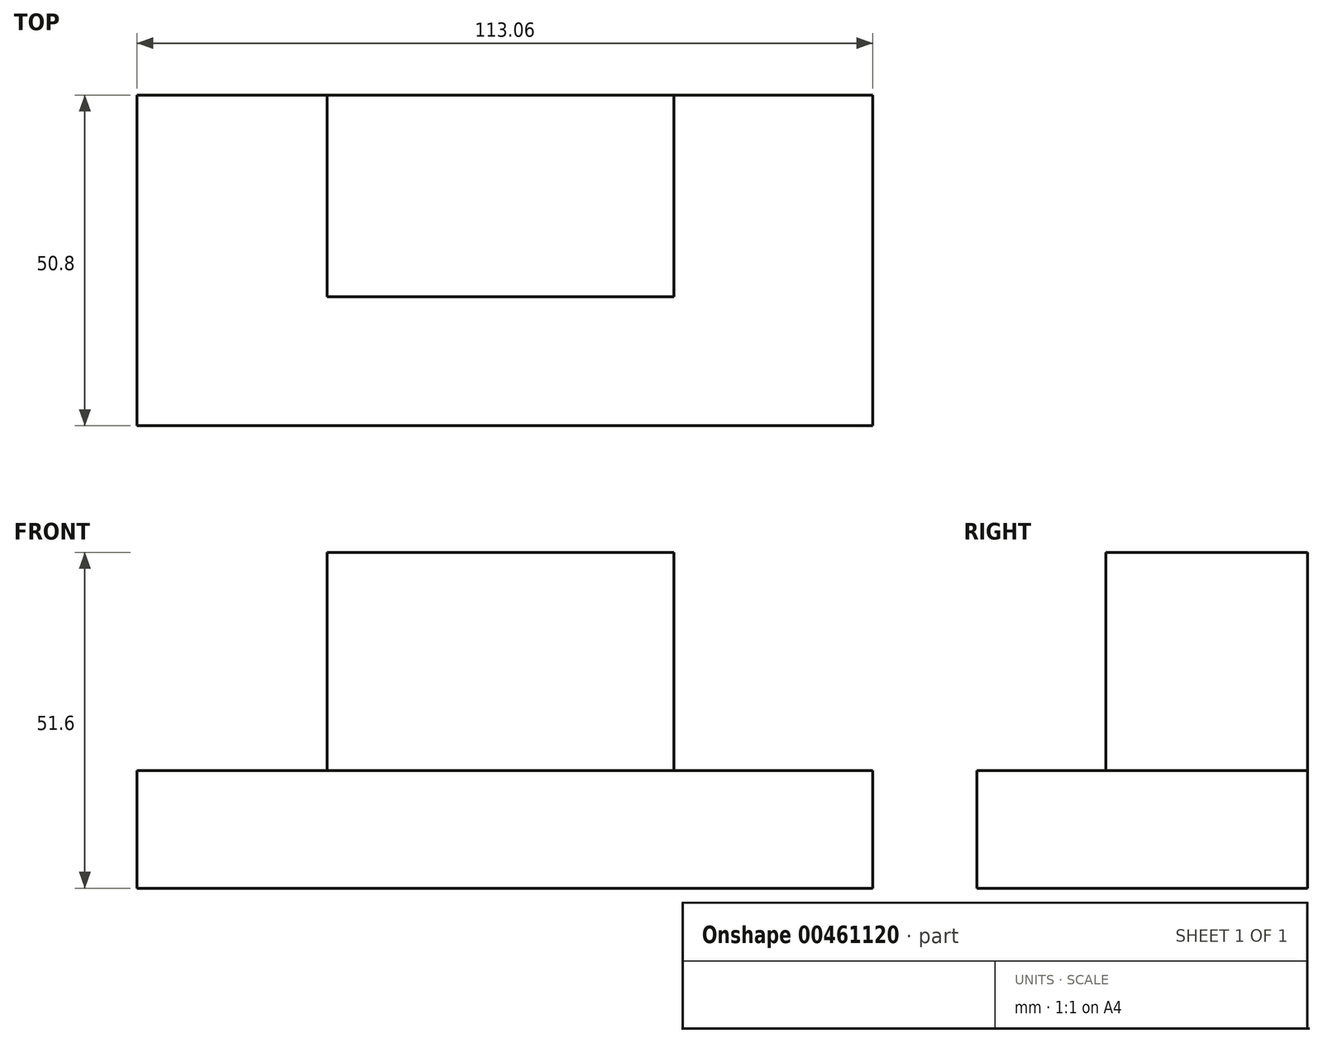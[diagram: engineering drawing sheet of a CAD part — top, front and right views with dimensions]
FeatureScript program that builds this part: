
annotation { "Feature Type Name" : "Feature", "Feature Type Description" : "" }
export const myFeature = defineFeature(function(context is Context, id is Id, definition is map)
    precondition{}
    {
        {
            var Q0;
            Q0=qCreatedBy(makeId("Front.planeOp"),FACE);
            var sketch = newSketch(context, id + "F0", { "sketchPlane" : qUnion([Q0])});
            skLineSegment(sketch, "E0.bottom", {"start": v(0, 0) * mm, "end": v(127.53, 0) * mm});
            skLineSegment(sketch, "E0.top", {"start": v(0, 50.83) * mm, "end": v(127.53, 50.83) * mm});
            skLineSegment(sketch, "E0.left", {"start": v(0, 0) * mm, "end": v(0, 50.83) * mm});
            skLineSegment(sketch, "E0.right", {"start": v(127.53, 0) * mm, "end": v(127.53, 50.83) * mm});
            skSolve(sketch);
        }
        {
            var Q0;
            Q0 = qSketchRegion(id + "F0", true);
            extrude(context, id + "F1", {"entities" : qUnion([Q0]), "depth" : 50.8 * mm});
        }
        {
            var Q0;
            Q0=makeQuery(id+"F1.opExtrude","SWEPT_FACE",FACE,{"disambiguationData":[OSD([sQuery(id+"F0.wireOp",EDGE,"E0.top")])]});
            extrude(context, id + "F2", {"entities" : qUnion([Q0]), "operationType" : NewBodyOperationType.REMOVE, "oppositeDirection" : true, "depth" : 32.77 * mm});
        }
        {
            var Q0;
            Q0=makeQuery(id+"F2.boolean.opBoolean","COPY",FACE,{"derivedFrom":makeQuery(id+"F2.opExtrude","CAP_FACE",FACE,{"disambiguationData":[OSD([sQuery(id+"F0.wireOp",EDGE,"E0.top")])],"isStart":false})});
            var sketch = newSketch(context, id + "F3", { "sketchPlane" : qUnion([Q0])});
            skLineSegment(sketch, "E1.bottom", {"start": v(38.9, 0) * mm, "end": v(92.14, 0) * mm});
            skLineSegment(sketch, "E1.top", {"start": v(38.9, -30.99) * mm, "end": v(92.14, -30.99) * mm});
            skLineSegment(sketch, "E1.left", {"start": v(38.9, 0) * mm, "end": v(38.9, -30.99) * mm});
            skLineSegment(sketch, "E1.right", {"start": v(92.14, 0) * mm, "end": v(92.14, -30.99) * mm});
            skSolve(sketch);
        }
        {
            var Q0;
            Q0=makeQuery(id+"F3.imprint","IMPRINT",FACE,{"disambiguationData":[TD([[makeQuery(id+"F3.imprint","IMPRINT",EDGE,{"derivedFrom":sQuery(id+"F3.wireOp",EDGE,"E1.bottom")}),-1.0]])]});
            extrude(context, id + "F4", {"entities" : qUnion([Q0]), "operationType" : NewBodyOperationType.ADD, "depth" : 33.53 * mm});
        }
        {
            var Q0;
            Q0=makeQuery(id+"F1.opExtrude","SWEPT_FACE",FACE,{"disambiguationData":[OSD([sQuery(id+"F0.wireOp",EDGE,"E0.right")])]});
            extrude(context, id + "F5", {"entities" : qUnion([Q0]), "operationType" : NewBodyOperationType.REMOVE, "oppositeDirection" : true, "depth" : 4.83 * mm});
        }
        {
            var Q0;
            Q0=makeQuery(id+"F1.opExtrude","SWEPT_FACE",FACE,{"disambiguationData":[OSD([sQuery(id+"F0.wireOp",EDGE,"E0.left")])]});
            extrude(context, id + "F6", {"entities" : qUnion([Q0]), "operationType" : NewBodyOperationType.ADD, "oppositeDirection" : true, "depth" : 7.37 * mm});
        }
        {
            var Q0;
            Q0=makeQuery(id+"F1.opExtrude","SWEPT_FACE",FACE,{"disambiguationData":[OSD([sQuery(id+"F0.wireOp",EDGE,"E0.left")])]});
            extrude(context, id + "F7", {"entities" : qUnion([Q0]), "operationType" : NewBodyOperationType.ADD, "oppositeDirection" : true, "depth" : 8.9 * mm});
        }
        {
            var Q0;
            Q0=makeQuery(id+"F1.opExtrude","SWEPT_FACE",FACE,{"disambiguationData":[OSD([sQuery(id+"F0.wireOp",EDGE,"E0.left")])]});
            extrude(context, id + "F8", {"entities" : qUnion([Q0]), "operationType" : NewBodyOperationType.REMOVE, "oppositeDirection" : true, "depth" : 9.65 * mm});
        }
        {
            var Q0;
            Q0=makeQuery(id+"F1.opExtrude","CAP_FACE",FACE,{"disambiguationData":[OSD([sQuery(id+"F0.wireOp",EDGE,"E0.bottom"),sQuery(id+"F0.wireOp",EDGE,"E0.top"),sQuery(id+"F0.wireOp",EDGE,"E0.left"),sQuery(id+"F0.wireOp",EDGE,"E0.right")])],"isStart":false});
            extrude(context, id + "F9", {"entities" : qUnion([Q0]), "operationType" : NewBodyOperationType.ADD, "oppositeDirection" : true, "depth" : 5.33 * mm});
        }
    });
